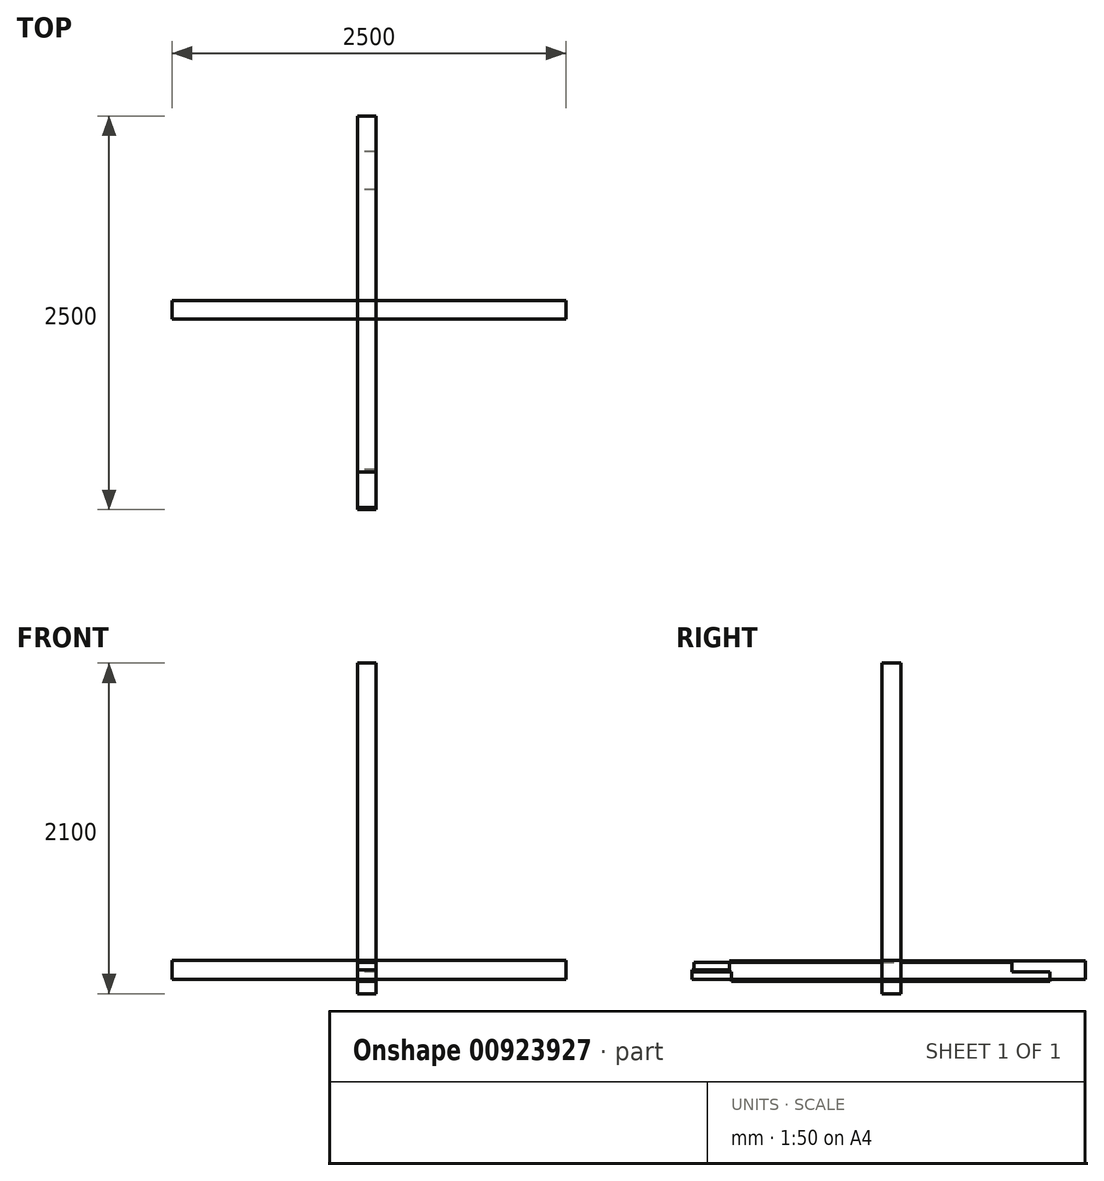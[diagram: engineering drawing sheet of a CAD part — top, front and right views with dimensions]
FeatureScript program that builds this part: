
annotation { "Feature Type Name" : "Feature", "Feature Type Description" : "" }
export const myFeature = defineFeature(function(context is Context, id is Id, definition is map)
    precondition{}
    {
        {
            var Q0;
            Q0=qCreatedBy(makeId("Right.planeOp"),FACE);
            var sketch = newSketch(context, id + "F0", { "sketchPlane" : qUnion([Q0])});
            skLineSegment(sketch, "E0.bottom", {"start": v(-1255.31, -9.02) * mm, "end": v(764.69, -9.02) * mm});
            skLineSegment(sketch, "E0.left", {"start": v(-1255.31, -9.02) * mm, "end": v(-1255.31, -69.02) * mm});
            skLineSegment(sketch, "E1", {"start": v(-1255.31, -69.02) * mm, "end": v(-1015.31, -69.02) * mm});
            skLineSegment(sketch, "E2", {"start": v(1004.69, -69.02) * mm, "end": v(1004.69, -129.02) * mm});
            skLineSegment(sketch, "E3", {"start": v(1004.69, -69.02) * mm, "end": v(764.69, -69.02) * mm});
            skLineSegment(sketch, "E4", {"start": v(764.69, -69.02) * mm, "end": v(764.69, -9.02) * mm});
            skLineSegment(sketch, "E5", {"start": v(-1015.31, -69.02) * mm, "end": v(-1015.31, -129.02) * mm});
            skLineSegment(sketch, "E6", {"start": v(-1015.31, -129.02) * mm, "end": v(1004.69, -129.02) * mm});
            skSolve(sketch);
        }
        {
            var Q0;
            Q0=makeQuery(id+"F0.imprint","IMPRINT",FACE,{"disambiguationData":[TD([[makeQuery(id+"F0.imprint","IMPRINT",EDGE,{"derivedFrom":sQuery(id+"F0.wireOp",EDGE,"E0.bottom")}),-1.0]])]});
            extrude(context, id + "F1", {"entities" : qUnion([Q0]), "endBound" : BoundingType.SYMMETRIC, "depth" : 120 * mm, "offsetDistance" : 25 * mm});
        }
        {
            var Q0;
            Q0=qCreatedBy(makeId("Right.planeOp"),FACE);
            var sketch = newSketch(context, id + "F2", { "sketchPlane" : qUnion([Q0])});
            skLineSegment(sketch, "E7.top", {"start": v(-1268.76, -116.78) * mm, "end": v(1231.24, -116.78) * mm});
            skLineSegment(sketch, "E7.right", {"start": v(1231.24, 3.22) * mm, "end": v(1231.24, -116.78) * mm});
            skLineSegment(sketch, "E8", {"start": v(-1268.76, -56.78) * mm, "end": v(-1268.76, -116.78) * mm});
            skLineSegment(sketch, "E9", {"start": v(-1268.76, -56.78) * mm, "end": v(-1028.76, -56.78) * mm});
            skLineSegment(sketch, "E10", {"start": v(-1028.76, -56.78) * mm, "end": v(-1028.76, 3.22) * mm});
            skLineSegment(sketch, "E11", {"start": v(-1028.76, 3.22) * mm, "end": v(1231.24, 3.22) * mm});
            skSolve(sketch);
        }
        {
            var Q0;
            Q0=makeQuery(id+"F2.imprint","IMPRINT",FACE,{"disambiguationData":[TD([[makeQuery(id+"F2.imprint","IMPRINT",EDGE,{"derivedFrom":sQuery(id+"F2.wireOp",EDGE,"E7.top")}),1.0]])]});
            extrude(context, id + "F3", {"entities" : qUnion([Q0]), "endBound" : BoundingType.SYMMETRIC, "depth" : 120 * mm, "offsetDistance" : 25 * mm});
        }
        {
            var Q0;
            Q0=qCreatedBy(makeId("Front.planeOp"),FACE);
            var sketch = newSketch(context, id + "F4", { "sketchPlane" : qUnion([Q0])});
            skLineSegment(sketch, "E12.bottom", {"start": v(-1235.6, 4.37) * mm, "end": v(1264.4, 4.37) * mm});
            skLineSegment(sketch, "E12.top", {"start": v(-1235.6, -115.63) * mm, "end": v(1264.4, -115.63) * mm});
            skLineSegment(sketch, "E12.left", {"start": v(-1235.6, 4.37) * mm, "end": v(-1235.6, -115.63) * mm});
            skLineSegment(sketch, "E12.right", {"start": v(1264.4, 4.37) * mm, "end": v(1264.4, -115.63) * mm});
            skSolve(sketch);
        }
        {
            var Q0;
            Q0=makeQuery(id+"F4.imprint","IMPRINT",FACE,{"disambiguationData":[TD([[makeQuery(id+"F4.imprint","IMPRINT",EDGE,{"derivedFrom":sQuery(id+"F4.wireOp",EDGE,"E12.bottom")}),-1.0]])]});
            extrude(context, id + "F5", {"entities" : qUnion([Q0]), "endBound" : BoundingType.SYMMETRIC, "depth" : 120 * mm, "offsetDistance" : 25 * mm});
        }
        {
            var Q0;
            Q0=qCreatedBy(makeId("Right.planeOp"),FACE);
            var sketch = newSketch(context, id + "F6", { "sketchPlane" : qUnion([Q0])});
            skLineSegment(sketch, "E13.bottom", {"start": v(-59.72, 1893.4) * mm, "end": v(60.28, 1893.4) * mm});
            skLineSegment(sketch, "E13.top", {"start": v(-59.72, -206.6) * mm, "end": v(60.28, -206.6) * mm});
            skLineSegment(sketch, "E13.left", {"start": v(-59.72, 1893.4) * mm, "end": v(-59.72, -206.6) * mm});
            skLineSegment(sketch, "E13.right", {"start": v(60.28, 1893.4) * mm, "end": v(60.28, -206.6) * mm});
            skSolve(sketch);
        }
        {
            var Q0;
            Q0=makeQuery(id+"F6.imprint","IMPRINT",FACE,{"disambiguationData":[TD([[makeQuery(id+"F6.imprint","IMPRINT",EDGE,{"derivedFrom":sQuery(id+"F6.wireOp",EDGE,"E13.bottom")}),-1.0]])]});
            extrude(context, id + "F7", {"entities" : qUnion([Q0]), "endBound" : BoundingType.SYMMETRIC, "depth" : 120 * mm, "offsetDistance" : 25 * mm});
        }
        {
            var Q0;
            Q0=makeQuery(id+"F1.opExtrude","SWEPT_FACE",FACE,{"disambiguationData":[OSD([sQuery(id+"F0.wireOp",EDGE,"E0.bottom")])]});
            var sketch = newSketch(context, id + "F8", { "sketchPlane" : qUnion([Q0])});
            skLineSegment(sketch, "E14", {"start": v(0, -1255.31) * mm, "end": v(0, -1135.41) * mm, "construction": true});
            skLineSegment(sketch, "E15", {"start": v(60, -1135.41) * mm, "end": v(-60, -1135.41) * mm, "construction": true});
            skLineSegment(sketch, "E16", {"start": v(0, -1135.41) * mm, "end": v(0, -1015.52) * mm, "construction": true});
            skSolve(sketch);
        }
        {
            var Q0;
            Q0=makeQuery(id+"F3.opExtrude","SWEPT_FACE",FACE,{"disambiguationData":[OSD([sQuery(id+"F2.wireOp",EDGE,"E7.top")])]});
            var sketch = newSketch(context, id + "F9", { "sketchPlane" : qUnion([Q0])});
            skLineSegment(sketch, "E17", {"start": v(0, 1268.76) * mm, "end": v(0, 1028.77) * mm, "construction": true});
            skPoint(sketch, "E18.startSnap0", {"position": v(0, 1148.77) * mm});
            skLineSegment(sketch, "E19", {"start": v(60, 1148.77) * mm, "end": v(-60, 1148.77) * mm, "construction": true});
            skLineSegment(sketch, "E20", {"start": v(0, -1231.24) * mm, "end": v(0, -871.24) * mm, "construction": true});
            skLineSegment(sketch, "E21", {"start": v(-60, -871.24) * mm, "end": v(60, -871.24) * mm, "construction": true});
            skSolve(sketch);
        }
        {
            var Q0;
            Q0=makeQuery(id+"F3.opExtrude","SWEPT_FACE",FACE,{"disambiguationData":[OSD([sQuery(id+"F2.wireOp",EDGE,"E11")])]});
            var sketch = newSketch(context, id + "F10", { "sketchPlane" : qUnion([Q0])});
            skLineSegment(sketch, "E22.0", {"start": v(-60, 871.24) * mm, "end": v(60, 871.24) * mm, "construction": true});
            skLineSegment(sketch, "E22.1", {"start": v(0, 1231.24) * mm, "end": v(0, 871.24) * mm, "construction": true});
            skSolve(sketch);
        }
        {
            var Q0;
            Q0=makeQuery(id+"F3.opExtrude","CAP_FACE",FACE,{"disambiguationData":[OSD([sQuery(id+"F2.wireOp",EDGE,"E7.top"),sQuery(id+"F2.wireOp",EDGE,"E7.right"),sQuery(id+"F2.wireOp",EDGE,"E8"),sQuery(id+"F2.wireOp",EDGE,"E9"),sQuery(id+"F2.wireOp",EDGE,"E10"),sQuery(id+"F2.wireOp",EDGE,"E11")])],"isStart":true});
            var sketch = newSketch(context, id + "F11", { "sketchPlane" : qUnion([Q0])});
            skLineSegment(sketch, "E23", {"start": v(-1231.24, -56.78) * mm, "end": v(-871.24, -56.78) * mm, "construction": true});
            skLineSegment(sketch, "E24", {"start": v(-871.24, 3.22) * mm, "end": v(-871.24, -116.78) * mm, "construction": true});
            skSolve(sketch);
        }
        {
            var Q0;
            Q0=makeQuery(id+"F3.opExtrude","CAP_FACE",FACE,{"disambiguationData":[OSD([sQuery(id+"F2.wireOp",EDGE,"E7.top"),sQuery(id+"F2.wireOp",EDGE,"E7.right"),sQuery(id+"F2.wireOp",EDGE,"E8"),sQuery(id+"F2.wireOp",EDGE,"E9"),sQuery(id+"F2.wireOp",EDGE,"E10"),sQuery(id+"F2.wireOp",EDGE,"E11")])],"isStart":false});
            var sketch = newSketch(context, id + "F12", { "sketchPlane" : qUnion([Q0])});
            skLineSegment(sketch, "E25.0", {"start": v(1231.24, -56.78) * mm, "end": v(871.24, -56.78) * mm, "construction": true});
            skLineSegment(sketch, "E25.1", {"start": v(871.24, 3.22) * mm, "end": v(871.24, -116.78) * mm, "construction": true});
            skSolve(sketch);
        }
        {
            var Q0;
            Q0=makeQuery(id+"F1.opExtrude","SWEPT_FACE",FACE,{"disambiguationData":[OSD([sQuery(id+"F0.wireOp",EDGE,"E6")])]});
            var sketch = newSketch(context, id + "F13", { "sketchPlane" : qUnion([Q0])});
            skPoint(sketch, "E26.startSnap0", {"position": v(0, -884.69) * mm});
            skLineSegment(sketch, "E27", {"start": v(0, -1004.69) * mm, "end": v(0, -884.69) * mm, "construction": true});
            skSolve(sketch);
        }
    });
